# Revit family: 2069269 Feilo Sylvania Lighting Fixture OFFICELYTE 1200 HE 4K SSH01 EM
name_source: partatom
category: Lighting Fixtures
revit_build: Autodesk Revit 2017 (Build: 20190507_1515(x64)
units: mm (PartAtom-declared; Revit-internal decimal feet)

## family parameters
Cut with Voids When Loaded = No
Host = Face
Light Source = Yes
OmniClass Number = 23.80.70.11.17
OmniClass Title = Specialized Lighting by Location or Use
Part Type = Normal
Room Calculation Point = No
Round Connector Dimension = Use Diameter
Shared = No

## types (1)
- 2069269 OFFICELYTE 1200 HE 4K SSH01 EM
    Apparent Load = 28 VA
    Assembly Code = D5020200
    Body Material = Steel_Sylvania_Officelyte LP LED_White_RAL 9016
    CRI ( Ra ) = 85
    Catalog Number = 2064456 OFFICELYTE LP LED HE 4K 600
    Color Filter = 16777215
    Default Elevation = 0 mm  [stored 0 ft]
    Description = The Concord OFFICELYTE LP LED HO 4K 600 is a high efficient luminaire for Office, education, meeting rooms. With efficacy of 95lm/W, at 4549lm, CRI of 85 and a very low glare ratio according to EN12464.
    Diffuser Material = Acrylic_Sylvania_Officelyte LP LED_Satin_4000K
    Dimming Lamp Color Temperature Shift = <None>
    Electrical Protection = CLASS I
    Emit Shape Visible in Rendering = No
    Emit from Rectangle Length = 564 mm
    Emit from Rectangle Width = 564 mm
    Glare Control = UGR <19
    Glow Wire Test = 650 °C
    Height = 95 mm
    IK Rating = IK02
    IP Rating = IP40
    Keynote = 16500
    LOR = 100 %
    Lamp = LED
    Length = 1197 mm  [stored 3.92717 ft]
    Life = 50 000 h
    Manufacturer = Havells-Sylvania Group
    Model = OFFICELYTE 1200 HE 4K SSH01 EM
    Photometric Web File = 2069269.ies
    Product Family = OFFICELYTE LP LED
    Product Page URL = http://www.sylvania-lighting.com
    Reflector Material = Steel_Sylvania_Officelyte LP LED_White_RAL 9016
    Tilt Angle = 90.00°
    URL = http://www.sylvania-lighting.com
    Voltage = 230 V
    Voltage Comments = UNV (Universal Voltage; 230-240 Volt)
    Weight = 5.90 kg
    Width = 297 mm  [stored 0.974409 ft]

note: [stored X ft] marks values corroborated as IEEE doubles in the binary element streams (Revit-internal decimal feet)

## geometry (parser evidence)
native form markers: Sweep x3
no freeform markers — native parametric forms only
